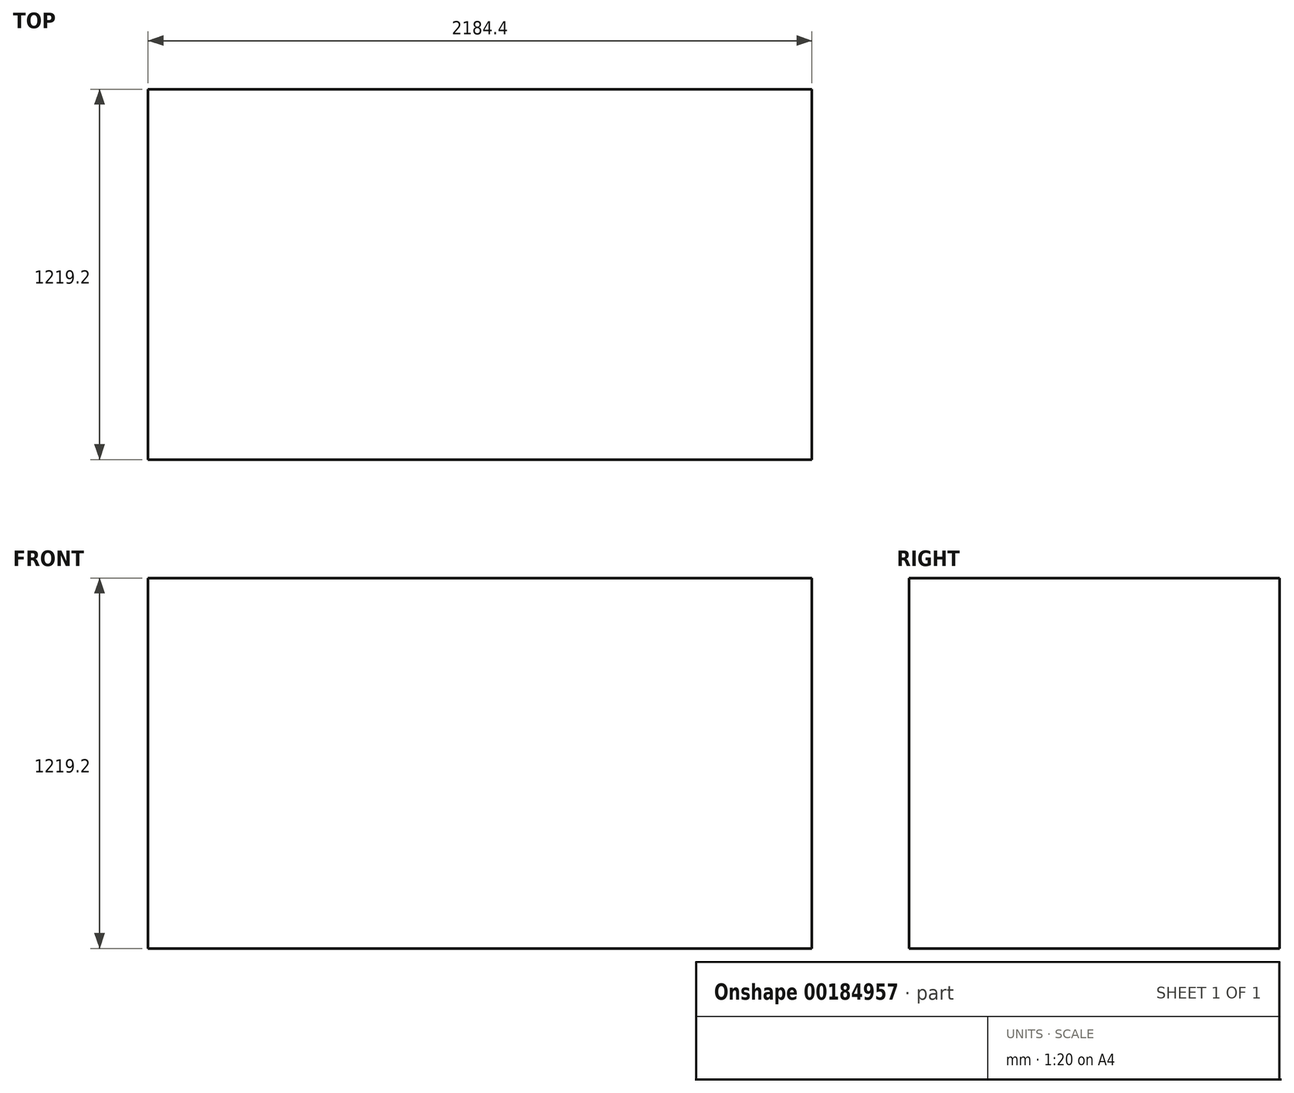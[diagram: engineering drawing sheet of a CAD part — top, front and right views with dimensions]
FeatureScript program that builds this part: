
annotation { "Feature Type Name" : "Feature", "Feature Type Description" : "" }
export const myFeature = defineFeature(function(context is Context, id is Id, definition is map)
    precondition{}
    {
        {
            var Q0;
            Q0=qCreatedBy(makeId("Top.planeOp"),FACE);
            var sketch = newSketch(context, id + "F0", { "sketchPlane" : qUnion([Q0])});
            skLineSegment(sketch, "E0.bottom", {"start": v(-2184.4, 609.6) * mm, "end": v(0, 609.6) * mm});
            skLineSegment(sketch, "E0.top", {"start": v(-2184.4, -609.6) * mm, "end": v(0, -609.6) * mm});
            skLineSegment(sketch, "E0.left", {"start": v(-2184.4, 609.6) * mm, "end": v(-2184.4, -609.6) * mm});
            skLineSegment(sketch, "E0.right", {"start": v(0, 609.6) * mm, "end": v(0, -609.6) * mm});
            skSolve(sketch);
        }
        {
            var Q0;
            Q0=makeQuery(id+"F0.imprint","IMPRINT",FACE,{"disambiguationData":[TD([[makeQuery(id+"F0.imprint","IMPRINT",EDGE,{"derivedFrom":sQuery(id+"F0.wireOp",EDGE,"E0.bottom")}),-1.0]])]});
            extrude(context, id + "F1", {"entities" : qUnion([Q0]), "depth" : 1219.2 * mm});
        }
    });
